# Revit family: 6. Водяные нагреватели UTR WWN
name_source: partatom
category: Оборудование
revit_build: Autodesk Revit 2016 (Build: 20151209_0715(x64)
units: mm (PartAtom-declared; Revit-internal decimal feet)

## family parameters
Всегда вертикально = Да
На основе рабочей плоскости = Нет
Общий = Нет
При загрузке вырезать с полостями = Нет
Размер круглого соединителя = Использовать диаметр
Тип детали = Нормальный
Точка расчета площади = Нет

## types (16) — shared parameters
h = 60 мм
Д = 350 мм
Д1 = 330 мм
Единица измерения = шт.
Завод изготовитель = KORF
Ключевая пометка = Вентиляция
Наименование и тех.хар-ка = Секция водяного нагревателя
Раздел = ОВ
Синий = Синий
высота ножек = 50 мм

## per-type parameters (varying)
| type | А | А1 | Б | Б1 | Г | Заправочный объем, л | Масса единицы | Материал | Теплопроизводительность, кВт | Тип, марка, обозначение | высота | размер В | ширина |
| 50-25 WWN/2 | 710 мм | 690 мм | 470 мм | 450 мм | 395 мм | 1 м³ | 25 | Сталь серая | 26 кВт | UTR 50-25 WWN/2 | 250 мм | 635 мм | 500 мм |
| 50-25 WWN/3 | 710 мм | 690 мм | 470 мм | 450 мм | 395 мм | 1.4 м³ | 27 | Сталь серая | 31 кВт | UTR 50-25 WWN/3 | 250 мм | 635 мм | 500 мм |
| 50-30 WWN/2 | 710 мм | 690 мм | 520 мм | 500 мм | 445 мм | 1.3 м³ | 26 | Сталь серая | 31 кВт | UTR 50-30 WWN/2 | 300 мм | 635 мм | 500 мм |
| 50-30 WWN/3 | 710 мм | 690 мм | 520 мм | 500 мм | 445 мм | 1.8 м³ | 27,5 | Сталь серая | 37 кВт | UTR 50-30 WWN/3 | 300 мм | 635 мм | 500 мм |
| 60-30 WWN/2 | 810 мм | 790 мм | 520 мм | 500 мм | 445 мм | 1.5 м³ | 29 | Сталь серая | 37 кВт | UTR 60-30 WWN/2 | 300 мм | 735 мм | 600 мм |
| 60-30 WWN/3 | 810 мм | 790 мм | 520 мм | 500 мм | 445 мм | 2 м³ | 30 | Сталь серая | 45 кВт | UTR 60-30 WWN/3 | 300 мм | 735 мм | 600 мм |
| 60-35 WWN/2 | 810 мм | 790 мм | 570 мм | 550 мм | 495 мм | 1.7 м³ | 31 | RAL 0000 Серый металл | 44 кВт | UTR 60-35 WWN/2 | 350 мм | 735 мм | 600 мм |
| 60-35 WWN/3 | 810 мм | 790 мм | 570 мм | 550 мм | 495 мм | 2.3 м³ | 32,5 | Сталь серая | 53 кВт | UTR 60-35 WWN/3 | 350 мм | 735 мм | 600 мм |
| 70-40 WWN/2 | 910 мм | 890 мм | 620 мм | 600 мм | 545 мм | 2.2 м³ | 33,5 | Сталь серая | 59 кВт | UTR 70-40 WWN/2 | 400 мм | 835 мм | 700 мм |
| 70-40 WWN/3 | 910 мм | 890 мм | 620 мм | 600 мм | 545 мм | 3 м³ | 36,5 | Сталь серая | 71 кВт | UTR 70-40 WWN/3 | 400 мм | 835 мм | 700 мм |
| 80-50 WWN/2 | 1010 мм | 990 мм | 720 мм | 700 мм | 645 мм | 3.2 м³ | 39 | Сталь серая | 83 кВт | UTR 80-50 WWN/2 | 500 мм | 935 мм | 800 мм |
| 80-50 WWN/3 | 1010 мм | 990 мм | 720 мм | 700 мм | 645 мм | 4.4 м³ | 43 | Сталь серая | 100 кВт | UTR 80-50 WWN/3 | 500 мм | 935 мм | 800 мм |
| 90-50 WWN/2 | 1125 мм | 1105 мм | 740 мм | 720 мм | 645 мм | 3.5 м³ | 43 | Сталь серая | 93 кВт | UTR 90-50 WWN/2 | 500 мм | 1050 мм | 900 мм |
| 90-50 WWN/3 | 1125 мм | 1105 мм | 740 мм | 720 мм | 645 мм | 4.8 м³ | 47 | Сталь серая | 112 кВт | UTR 90-50 WWN/3 | 500 мм | 1050 мм | 900 мм |
| 100-50 WWN/2 | 1225 мм | 1205 мм | 740 мм | 720 мм | 665 мм | 3.8 м³ | 45,5 | Сталь серая | 102 кВт | UTR 100-50 WWN/2 | 500 мм | 1150 мм | 1000 мм |
| 100-50 WWN/3 | 1225 мм | 1205 мм | 740 мм | 720 мм | 665 мм | 5.3 м³ | 50 | Сталь серая | 124 кВт | UTR 100-50 WWN/3 | 500 мм | 1150 мм | 1000 мм |
